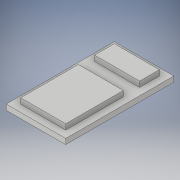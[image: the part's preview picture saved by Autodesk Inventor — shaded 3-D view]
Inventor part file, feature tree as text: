
AUTODESK INVENTOR PART (.ipt)
format: ipt  version: 2019 (Build 230136000, 136)  size: 117,248 bytes
history: native  units: mm
features: extrude x2, sketch x2
ambient origin geometry x8: Origin, YZ Plane, XZ Plane, XY Plane, X Axis, Y Axis, Z Axis, Center Point
bodies: Solid1 (feature_tree)
feature tree (4):
  extrude  "Extrusion1"  Depth=30.0mm
  extrude  "Extrusion2"  Depth=2.0mm
  sketch  "Sketch1"  dims[d0=16.5mm d1=30.0mm]
  sketch  "Sketch2"  dims[d2=1.5mm d3=0.0mm d4=2.0mm d5=2.0mm d6=16.0mm d7=2.0mm d8=5.5mm d9=1.5mm d10=0.0mm]
